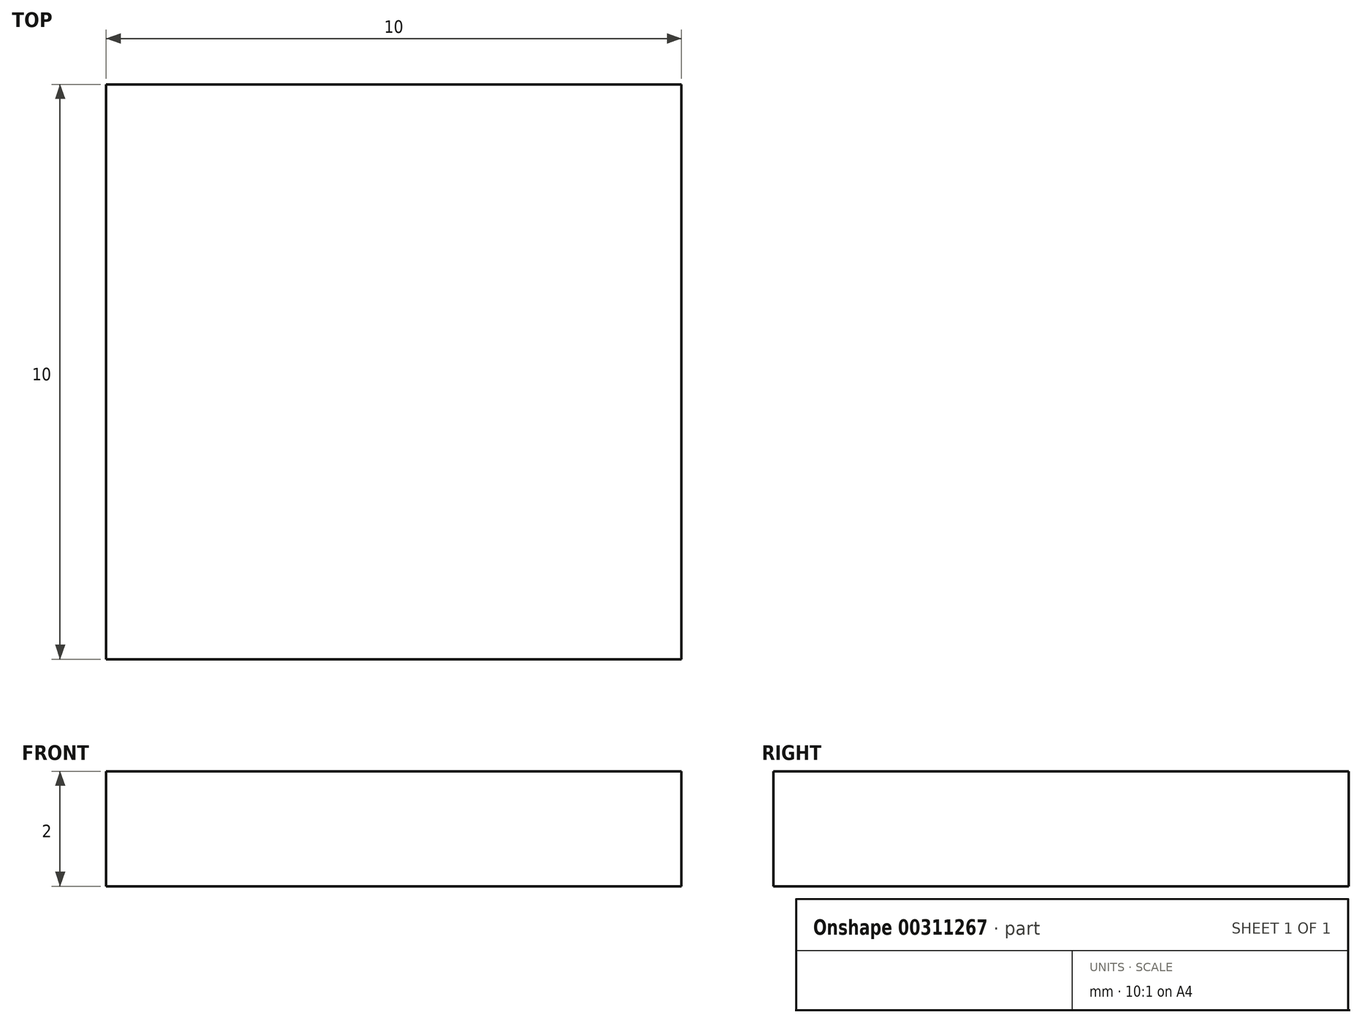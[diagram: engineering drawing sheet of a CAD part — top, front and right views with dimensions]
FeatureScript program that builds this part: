
annotation { "Feature Type Name" : "Feature", "Feature Type Description" : "" }
export const myFeature = defineFeature(function(context is Context, id is Id, definition is map)
    precondition{}
    {
        {
            var Q0;
            Q0=qCreatedBy(makeId("Top.planeOp"),FACE);
            var sketch = newSketch(context, id + "F0", { "sketchPlane" : qUnion([Q0])});
            skLineSegment(sketch, "E0.bottom", {"start": v(5, -5) * mm, "end": v(-5, -5) * mm});
            skLineSegment(sketch, "E0.top", {"start": v(5, 5) * mm, "end": v(-5, 5) * mm});
            skLineSegment(sketch, "E0.left", {"start": v(5, -5) * mm, "end": v(5, 5) * mm});
            skLineSegment(sketch, "E0.right", {"start": v(-5, -5) * mm, "end": v(-5, 5) * mm});
            skPoint(sketch, "E0.middle", {"position": v(0, 0) * mm});
            skSolve(sketch);
        }
        {
            var Q0;
            Q0=makeQuery(id+"F0.imprint","IMPRINT",FACE,{"disambiguationData":[TD([[makeQuery(id+"F0.imprint","IMPRINT",EDGE,{"derivedFrom":sQuery(id+"F0.wireOp",EDGE,"E0.bottom")}),-1.0]])]});
            extrude(context, id + "F1", {"entities" : qUnion([Q0]), "flatOperationType" : FlatOperationType.REMOVE, "offsetDistance" : 25.4 * mm, "depth" : 2 * mm, "domain" : OperationDomain.MODEL});
        }
    });
